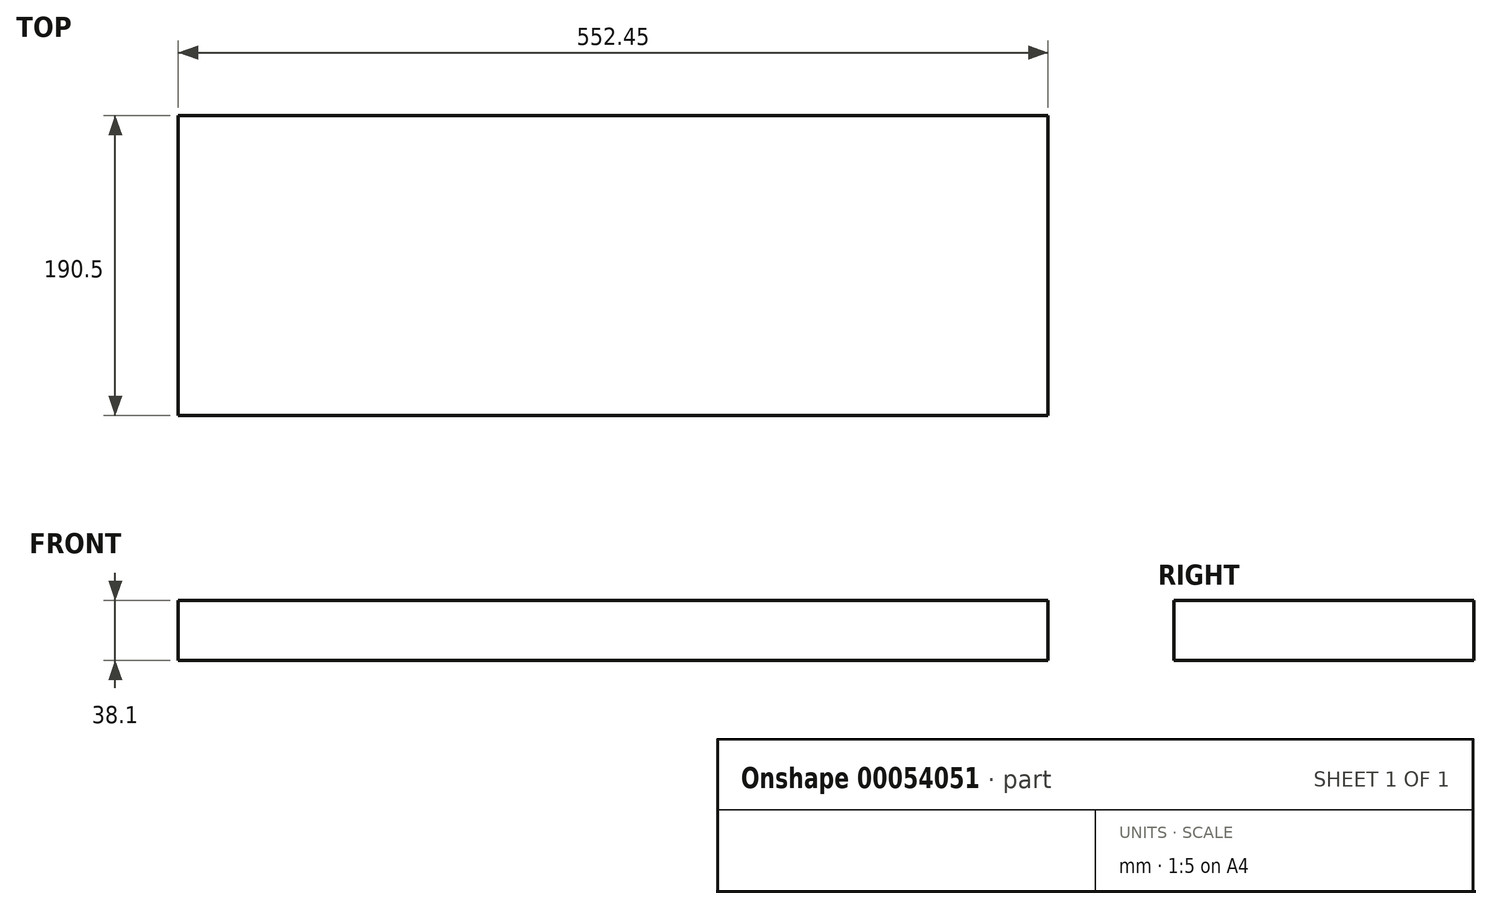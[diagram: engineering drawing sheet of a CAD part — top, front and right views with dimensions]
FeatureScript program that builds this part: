
annotation { "Feature Type Name" : "Feature", "Feature Type Description" : "" }
export const myFeature = defineFeature(function(context is Context, id is Id, definition is map)
    precondition{}
    {
        {
            var Q0;
            Q0=qCreatedBy(makeId("Right.planeOp"),FACE);
            var sketch = newSketch(context, id + "F0", { "sketchPlane" : qUnion([Q0])});
            skLineSegment(sketch, "E0.bottom", {"start": v(0, 0) * mm, "end": v(190.5, 0) * mm});
            skLineSegment(sketch, "E0.top", {"start": v(0, 38.1) * mm, "end": v(190.5, 38.1) * mm});
            skLineSegment(sketch, "E0.left", {"start": v(0, 0) * mm, "end": v(0, 38.1) * mm});
            skLineSegment(sketch, "E0.right", {"start": v(190.5, 0) * mm, "end": v(190.5, 38.1) * mm});
            skSolve(sketch);
        }
        {
            var Q0;
            Q0=makeQuery(id+"F0.imprint","IMPRINT",FACE,{"disambiguationData":[TD([[makeQuery(id+"F0.imprint","IMPRINT",EDGE,{"derivedFrom":sQuery(id+"F0.wireOp",EDGE,"E0.bottom")}),1.0]])]});
            extrude(context, id + "F1", {"entities" : qUnion([Q0]), "depth" : 552.45 * mm});
        }
    });
